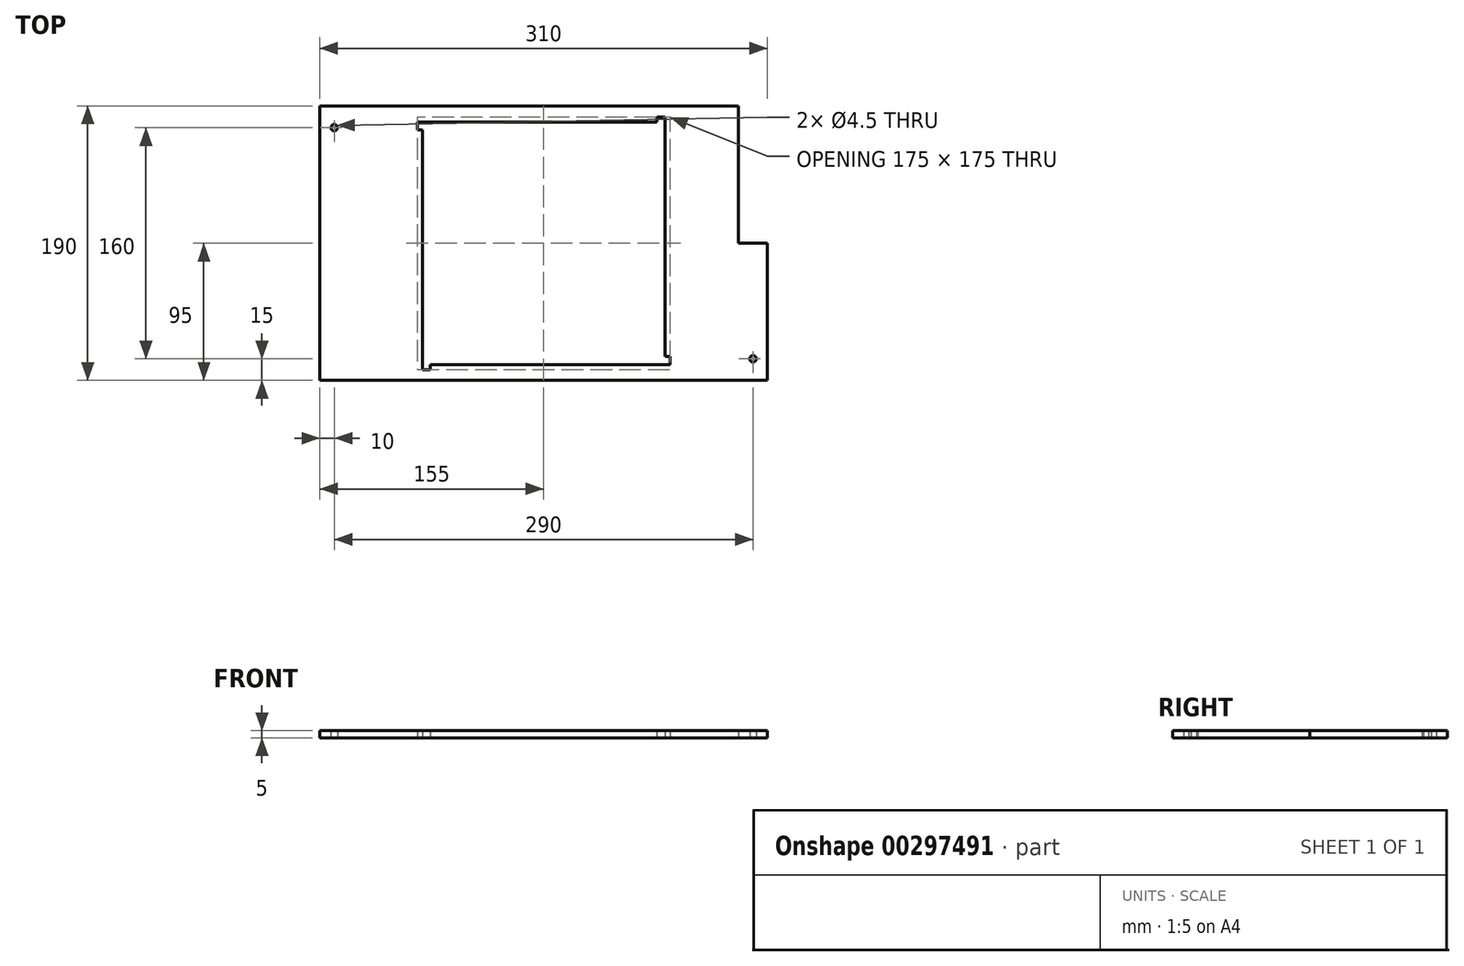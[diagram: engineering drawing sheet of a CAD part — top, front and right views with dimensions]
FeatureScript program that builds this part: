
annotation { "Feature Type Name" : "Feature", "Feature Type Description" : "" }
export const myFeature = defineFeature(function(context is Context, id is Id, definition is map)
    precondition{}
    {
        {
            var Q0;
            Q0=qCreatedBy(makeId("Top.planeOp"),FACE);
            var sketch = newSketch(context, id + "F0", { "sketchPlane" : qUnion([Q0])});
            skLineSegment(sketch, "E0.bottom", {"start": v(84, -84) * mm, "end": v(-78.5, -84) * mm});
            skLineSegment(sketch, "E0.top", {"start": v(78.5, 84) * mm, "end": v(-84, 84) * mm});
            skLineSegment(sketch, "E0.left", {"start": v(84, -78.5) * mm, "end": v(84, 84) * mm});
            skLineSegment(sketch, "E0.right", {"start": v(-84, -84) * mm, "end": v(-84, 78.5) * mm});
            skPoint(sketch, "E0.middle", {"position": v(0, 0) * mm});
            skLineSegment(sketch, "E1", {"start": v(84, -84) * mm, "end": v(87.5, -84) * mm});
            skLineSegment(sketch, "E2", {"start": v(87.5, -84) * mm, "end": v(87.5, -78.5) * mm});
            skLineSegment(sketch, "E3", {"start": v(87.5, -78.5) * mm, "end": v(84, -78.5) * mm});
            skLineSegment(sketch, "E4", {"start": v(84, 84) * mm, "end": v(84, 87.5) * mm});
            skLineSegment(sketch, "E5", {"start": v(84, 87.5) * mm, "end": v(78.5, 87.5) * mm});
            skLineSegment(sketch, "E6", {"start": v(78.5, 87.5) * mm, "end": v(78.5, 84) * mm});
            skLineSegment(sketch, "E7", {"start": v(-84, 84) * mm, "end": v(-87.5, 84) * mm});
            skLineSegment(sketch, "E8", {"start": v(-87.5, 84) * mm, "end": v(-87.5, 78.5) * mm});
            skLineSegment(sketch, "E9", {"start": v(-87.5, 78.5) * mm, "end": v(-84, 78.5) * mm});
            skLineSegment(sketch, "E10", {"start": v(-84, -84) * mm, "end": v(-84, -87.5) * mm});
            skLineSegment(sketch, "E11", {"start": v(-84, -87.5) * mm, "end": v(-78.5, -87.5) * mm});
            skLineSegment(sketch, "E12", {"start": v(-78.5, -87.5) * mm, "end": v(-78.5, -84) * mm});
            skLineSegment(sketch, "E13.bottom", {"start": v(155, -95) * mm, "end": v(-155, -95) * mm});
            skLineSegment(sketch, "E13.top", {"start": v(135, 95) * mm, "end": v(-155, 95) * mm});
            skLineSegment(sketch, "E13.left", {"start": v(155, -95) * mm, "end": v(155, 0) * mm});
            skLineSegment(sketch, "E13.right", {"start": v(-155, -95) * mm, "end": v(-155, 95) * mm});
            skCircle(sketch, "E14", {"center": v(-145, 80) * mm, "radius": 2.25 * mm});
            skCircle(sketch, "E15", {"center": v(145, -80) * mm, "radius": 2.25 * mm});
            skLineSegment(sketch, "E16", {"start": v(155, 0) * mm, "end": v(135, 0) * mm});
            skPoint(sketch, "E16.endSnap0", {"position": v(155, 0) * mm});
            skLineSegment(sketch, "E17", {"start": v(135, 0) * mm, "end": v(135, 95) * mm});
            skPoint(sketch, "E18", {"position": v(145, 0) * mm});
            skPoint(sketch, "E19.1.1", {"position": v(290, 0) * mm});
            skLineSegment(sketch, "E19.1.2", {"start": v(155, -95) * mm, "end": v(445, -95) * mm});
            skLineSegment(sketch, "E19.1.3", {"start": v(445, 95) * mm, "end": v(445, -95) * mm});
            skLineSegment(sketch, "E19.1.4", {"start": v(206, 78.5) * mm, "end": v(206, -84) * mm});
            skLineSegment(sketch, "E19.1.5", {"start": v(374, 84) * mm, "end": v(374, -78.5) * mm});
            skLineSegment(sketch, "E19.1.6", {"start": v(206, 84) * mm, "end": v(368.5, 84) * mm});
            skLineSegment(sketch, "E19.1.7", {"start": v(211.5, -84) * mm, "end": v(374, -84) * mm});
            skLineSegment(sketch, "E19.1.8", {"start": v(155, 0) * mm, "end": v(155, -95) * mm});
            skLineSegment(sketch, "E19.1.9", {"start": v(135, 95) * mm, "end": v(135, 0) * mm});
            skPoint(sketch, "E19.1.10", {"position": v(135, 0) * mm});
            skLineSegment(sketch, "E19.1.11", {"start": v(135, 95) * mm, "end": v(445, 95) * mm});
            skPoint(sketch, "E19.1.12", {"position": v(290, 0) * mm});
            skCircle(sketch, "E19.1.13", {"center": v(145, 80) * mm, "radius": 2.25 * mm});
            skLineSegment(sketch, "E19.1.14", {"start": v(206, -84) * mm, "end": v(206, -87.5) * mm});
            skLineSegment(sketch, "E19.1.15", {"start": v(206, -87.5) * mm, "end": v(211.5, -87.5) * mm});
            skLineSegment(sketch, "E19.1.16", {"start": v(135, 0) * mm, "end": v(155, 0) * mm});
            skLineSegment(sketch, "E19.1.17", {"start": v(211.5, -87.5) * mm, "end": v(211.5, -84) * mm});
            skCircle(sketch, "E19.1.18", {"center": v(435, -80) * mm, "radius": 2.25 * mm});
            skLineSegment(sketch, "E19.1.19", {"start": v(202.5, 78.5) * mm, "end": v(206, 78.5) * mm});
            skLineSegment(sketch, "E19.1.20", {"start": v(202.5, 84) * mm, "end": v(202.5, 78.5) * mm});
            skLineSegment(sketch, "E19.1.21", {"start": v(374, 84) * mm, "end": v(374, 87.5) * mm});
            skLineSegment(sketch, "E19.1.22", {"start": v(377.5, -78.5) * mm, "end": v(374, -78.5) * mm});
            skLineSegment(sketch, "E19.1.23", {"start": v(368.5, 87.5) * mm, "end": v(368.5, 84) * mm});
            skLineSegment(sketch, "E19.1.24", {"start": v(374, -84) * mm, "end": v(377.5, -84) * mm});
            skLineSegment(sketch, "E19.1.25", {"start": v(377.5, -84) * mm, "end": v(377.5, -78.5) * mm});
            skLineSegment(sketch, "E19.1.26", {"start": v(206, 84) * mm, "end": v(202.5, 84) * mm});
            skLineSegment(sketch, "E19.1.27", {"start": v(374, 87.5) * mm, "end": v(368.5, 87.5) * mm});
            skSolve(sketch);
        }
        {
            var Q0;
            Q0=makeQuery(id+"F0.imprint","IMPRINT",FACE,{"disambiguationData":[TD([[makeQuery(id+"F0.imprint","IMPRINT",EDGE,{"derivedFrom":sQuery(id+"F0.wireOp",EDGE,"E0.bottom")}),1.0]])]});
            extrude(context, id + "F1", {"entities" : qUnion([Q0]), "depth" : 5 * mm});
        }
    });
